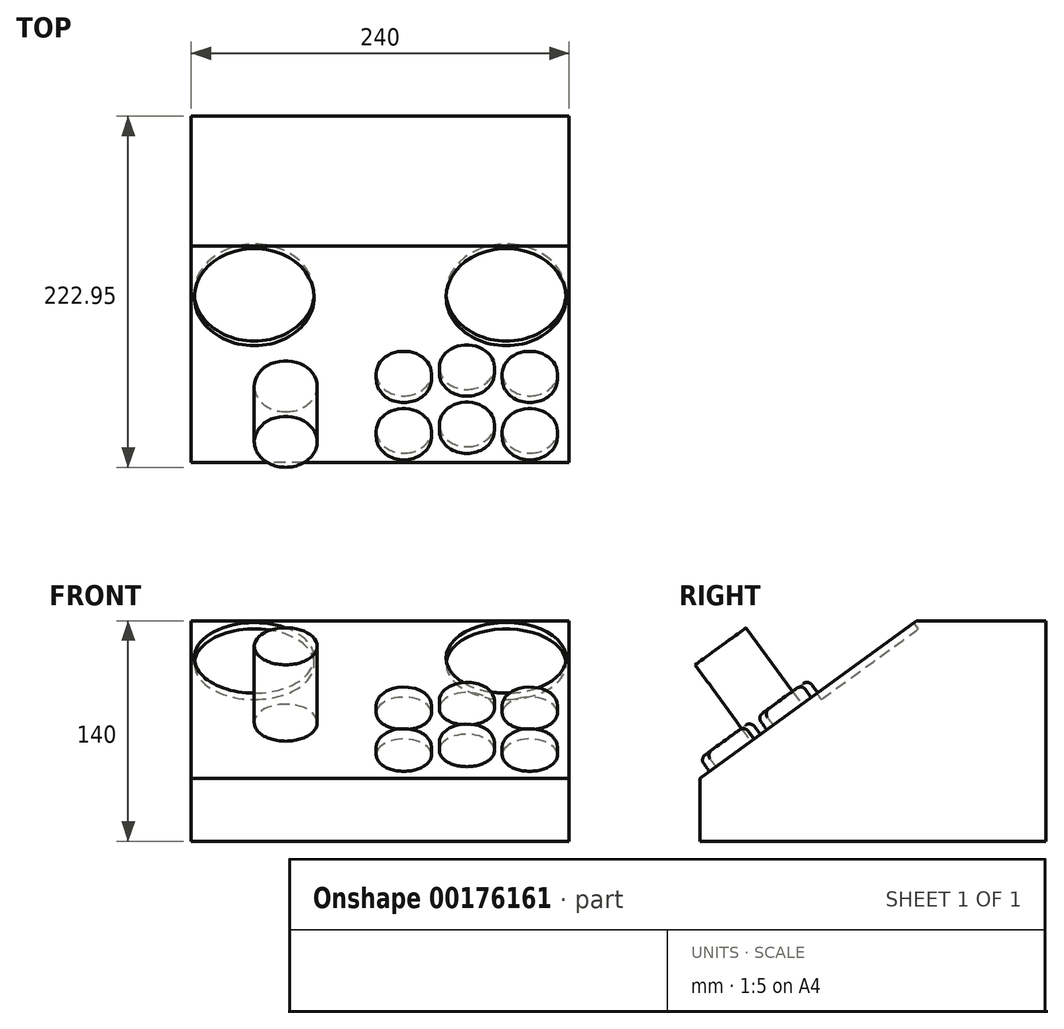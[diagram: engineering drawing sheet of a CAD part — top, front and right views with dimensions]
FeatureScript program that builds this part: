
annotation { "Feature Type Name" : "Feature", "Feature Type Description" : "" }
export const myFeature = defineFeature(function(context is Context, id is Id, definition is map)
    precondition{}
    {
        {
            var Q0;
            Q0=qCreatedBy(makeId("Right.planeOp"),FACE);
            var sketch = newSketch(context, id + "F0", { "sketchPlane" : qUnion([Q0])});
            skLineSegment(sketch, "E0.bottom", {"start": v(27.48, 50) * mm, "end": v(110, 50) * mm});
            skLineSegment(sketch, "E0.top", {"start": v(-110, -50) * mm, "end": v(110, -50) * mm});
            skLineSegment(sketch, "E0.right", {"start": v(110, 50) * mm, "end": v(110, -50) * mm});
            skPoint(sketch, "E0.middle", {"position": v(0, 0) * mm});
            skLineSegment(sketch, "E1", {"start": v(-110, -50) * mm, "end": v(27.48, 50) * mm});
            skLineSegment(sketch, "E2", {"start": v(27.48, 50) * mm, "end": v(27.48, -50) * mm});
            skLineSegment(sketch, "E3.top", {"start": v(-110, -90) * mm, "end": v(110, -90) * mm});
            skLineSegment(sketch, "E3.left", {"start": v(-110, -50) * mm, "end": v(-110, -90) * mm});
            skLineSegment(sketch, "E3.right", {"start": v(110, -50) * mm, "end": v(110, -90) * mm});
            skPoint(sketch, "E4.orphan", {"position": v(-110, 50) * mm});
            skSolve(sketch);
        }
        {
            var Q0;
            {var subQ0=sQuery(id+"F0.wireOp",EDGE,"E1");Q0=makeQuery(id+"F0.imprint","IMPRINT",FACE,{"disambiguationData":[TD([[makeQuery(id+"F0.imprint","IMPRINT",EDGE,{"derivedFrom":subQ0}),-1.0]])]});}
            var Q1;
            Q1=makeQuery(id+"F0.imprint","IMPRINT",FACE,{"disambiguationData":[TD([[makeQuery(id+"F0.imprint","IMPRINT",EDGE,{"derivedFrom":sQuery(id+"F0.wireOp",EDGE,"E0.bottom")}),-1.0]])]});
            var Q2;
            Q2=makeQuery(id+"F0.imprint","IMPRINT",FACE,{"disambiguationData":[TD([[makeQuery(id+"F0.imprint","IMPRINT",EDGE,{"derivedFrom":sQuery(id+"F0.wireOp",EDGE,"E3.top")}),1.0]])]});
            extrude(context, id + "F1", {"entities" : qUnion([Q0, Q1, Q2]), "endBound" : BoundingType.SYMMETRIC, "depth" : 240 * mm, "offsetDistance" : 25 * mm});
        }
        {
            var Q0;
            Q0=makeQuery(id+"F1.opExtrude","SWEPT_FACE",FACE,{"disambiguationData":[OSD([sQuery(id+"F0.wireOp",EDGE,"E1")])]});
            var sketch = newSketch(context, id + "F2", { "sketchPlane" : qUnion([Q0])});
            skCircle(sketch, "E5", {"center": v(-60, -58.37) * mm, "radius": 20 * mm});
            skCircle(sketch, "E6", {"center": v(15, -93.37) * mm, "radius": 17.5 * mm});
            skCircle(sketch, "E7", {"center": v(15, -48.37) * mm, "radius": 17.5 * mm});
            skCircle(sketch, "E8", {"center": v(55, -88.37) * mm, "radius": 17.5 * mm});
            skCircle(sketch, "E9", {"center": v(55, -43.37) * mm, "radius": 17.5 * mm});
            skCircle(sketch, "E10", {"center": v(95, -48.37) * mm, "radius": 17.5 * mm});
            skCircle(sketch, "E11", {"center": v(95, -93.37) * mm, "radius": 17.5 * mm});
            skCircle(sketch, "E12", {"center": v(-80, 11.63) * mm, "radius": 38.1 * mm});
            skCircle(sketch, "E13", {"center": v(80, 11.63) * mm, "radius": 38.1 * mm});
            skLineSegment(sketch, "E14.bottom", {"start": v(25.4, 49.73) * mm, "end": v(-25.4, 49.73) * mm});
            skLineSegment(sketch, "E14.top", {"start": v(25.4, -26.47) * mm, "end": v(-25.4, -26.47) * mm});
            skLineSegment(sketch, "E14.left", {"start": v(25.4, 49.73) * mm, "end": v(25.4, -26.47) * mm});
            skLineSegment(sketch, "E14.right", {"start": v(-25.4, 49.73) * mm, "end": v(-25.4, -26.47) * mm});
            skPoint(sketch, "E14.middle", {"position": v(0, 11.63) * mm});
            skPoint(sketch, "E15.start.orphan", {"position": v(0, 56.63) * mm});
            skPoint(sketch, "E16.trimOffspring.end.orphan", {"position": v(0, -33.37) * mm});
            skLineSegment(sketch, "E17.bottom", {"start": v(-120, 51.63) * mm, "end": v(120, 51.63) * mm});
            skLineSegment(sketch, "E17.top", {"start": v(-120, -118.37) * mm, "end": v(120, -118.37) * mm});
            skLineSegment(sketch, "E17.left", {"start": v(-120, 51.63) * mm, "end": v(-120, -118.37) * mm});
            skLineSegment(sketch, "E17.right", {"start": v(120, 51.63) * mm, "end": v(120, -118.37) * mm});
            skSolve(sketch);
        }
        {
            var Q0;
            Q0=makeQuery(id+"F2.imprint","IMPRINT",FACE,{"disambiguationData":[TD([[makeQuery(id+"F2.imprint","IMPRINT",EDGE,{"derivedFrom":sQuery(id+"F2.wireOp",EDGE,"E12")}),1.0]])]});
            extrude(context, id + "F3", {"entities" : qUnion([Q0]), "operationType" : NewBodyOperationType.REMOVE, "oppositeDirection" : true, "depth" : 5 * mm, "offsetDistance" : 25 * mm});
        }
        {
            var Q0;
            Q0=makeQuery(id+"F2.imprint","IMPRINT",FACE,{"disambiguationData":[TD([[makeQuery(id+"F2.imprint","IMPRINT",EDGE,{"derivedFrom":sQuery(id+"F2.wireOp",EDGE,"E13")}),1.0]])]});
            extrude(context, id + "F4", {"entities" : qUnion([Q0]), "operationType" : NewBodyOperationType.REMOVE, "oppositeDirection" : true, "depth" : 5 * mm, "offsetDistance" : 25 * mm});
        }
        {
            var Q0;
            Q0=makeQuery(id+"F2.imprint","IMPRINT",FACE,{"disambiguationData":[TD([[makeQuery(id+"F2.imprint","IMPRINT",EDGE,{"derivedFrom":sQuery(id+"F2.wireOp",EDGE,"E7")}),1.0]])]});
            extrude(context, id + "F5", {"entities" : qUnion([Q0]), "operationType" : NewBodyOperationType.ADD, "depth" : 10 * mm, "offsetDistance" : 25 * mm});
        }
        {
            var Q0;
            Q0=makeQuery(id+"F2.imprint","IMPRINT",FACE,{"disambiguationData":[TD([[makeQuery(id+"F2.imprint","IMPRINT",EDGE,{"derivedFrom":sQuery(id+"F2.wireOp",EDGE,"E6")}),1.0]])]});
            var Q1;
            Q1=makeQuery(id+"F2.imprint","IMPRINT",FACE,{"disambiguationData":[TD([[makeQuery(id+"F2.imprint","IMPRINT",EDGE,{"derivedFrom":sQuery(id+"F2.wireOp",EDGE,"E9")}),1.0]])]});
            var Q2;
            Q2=makeQuery(id+"F2.imprint","IMPRINT",FACE,{"disambiguationData":[TD([[makeQuery(id+"F2.imprint","IMPRINT",EDGE,{"derivedFrom":sQuery(id+"F2.wireOp",EDGE,"E8")}),1.0]])]});
            var Q3;
            Q3=makeQuery(id+"F2.imprint","IMPRINT",FACE,{"disambiguationData":[TD([[makeQuery(id+"F2.imprint","IMPRINT",EDGE,{"derivedFrom":sQuery(id+"F2.wireOp",EDGE,"E10")}),1.0]])]});
            var Q4;
            Q4=makeQuery(id+"F2.imprint","IMPRINT",FACE,{"disambiguationData":[TD([[makeQuery(id+"F2.imprint","IMPRINT",EDGE,{"derivedFrom":sQuery(id+"F2.wireOp",EDGE,"E11")}),1.0]])]});
            extrude(context, id + "F6", {"entities" : qUnion([Q0, Q1, Q2, Q3, Q4]), "operationType" : NewBodyOperationType.ADD, "depth" : 10 * mm, "offsetDistance" : 25 * mm});
        }
        {
            var Q0;
            Q0=makeQuery(id+"F2.imprint","IMPRINT",FACE,{"disambiguationData":[TD([[makeQuery(id+"F2.imprint","IMPRINT",EDGE,{"derivedFrom":sQuery(id+"F2.wireOp",EDGE,"E5")}),1.0]])]});
            extrude(context, id + "F7", {"entities" : qUnion([Q0]), "operationType" : NewBodyOperationType.ADD, "depth" : 60 * mm, "offsetDistance" : 25 * mm});
        }
        {
            var Q0;
            Q0=makeQuery(id+"F5.opExtrude","CAP_EDGE",EDGE,{"disambiguationData":[OSD([sQuery(id+"F2.wireOp",EDGE,"E7")])],"isStart":false});
            fillet(context, id + "F8", {"entities" : qUnion([Q0]), "radius" : 4 * mm, "tangentPropagation" : true, "allowEdgeOverflow" : false});
        }
        {
            var Q0;
            Q0=makeQuery(id+"F6.opExtrude","CAP_EDGE",EDGE,{"disambiguationData":[OSD([sQuery(id+"F2.wireOp",EDGE,"E9")])],"isStart":false});
            var Q1;
            Q1=makeQuery(id+"F6.opExtrude","CAP_EDGE",EDGE,{"disambiguationData":[OSD([sQuery(id+"F2.wireOp",EDGE,"E10")])],"isStart":false});
            var Q2;
            Q2=makeQuery(id+"F6.opExtrude","CAP_EDGE",EDGE,{"disambiguationData":[OSD([sQuery(id+"F2.wireOp",EDGE,"E11")])],"isStart":false});
            var Q3;
            Q3=makeQuery(id+"F6.opExtrude","CAP_EDGE",EDGE,{"disambiguationData":[OSD([sQuery(id+"F2.wireOp",EDGE,"E8")])],"isStart":false});
            var Q4;
            Q4=makeQuery(id+"F6.opExtrude","CAP_EDGE",EDGE,{"disambiguationData":[OSD([sQuery(id+"F2.wireOp",EDGE,"E6")])],"isStart":false});
            fillet(context, id + "F9", {"entities" : qUnion([Q0, Q1, Q2, Q3, Q4]), "radius" : 4 * mm, "tangentPropagation" : true, "allowEdgeOverflow" : false});
        }
        {
            var Q0;
            Q0=sQuery(id+"F2.wireOp",EDGE,"E5");
            extrude(context, id + "F10", {"bodyType" : ToolBodyType.SURFACE, "surfaceEntities" : qUnion([Q0]), "depth" : 20 * mm, "offsetDistance" : 25 * mm});
        }
    });
